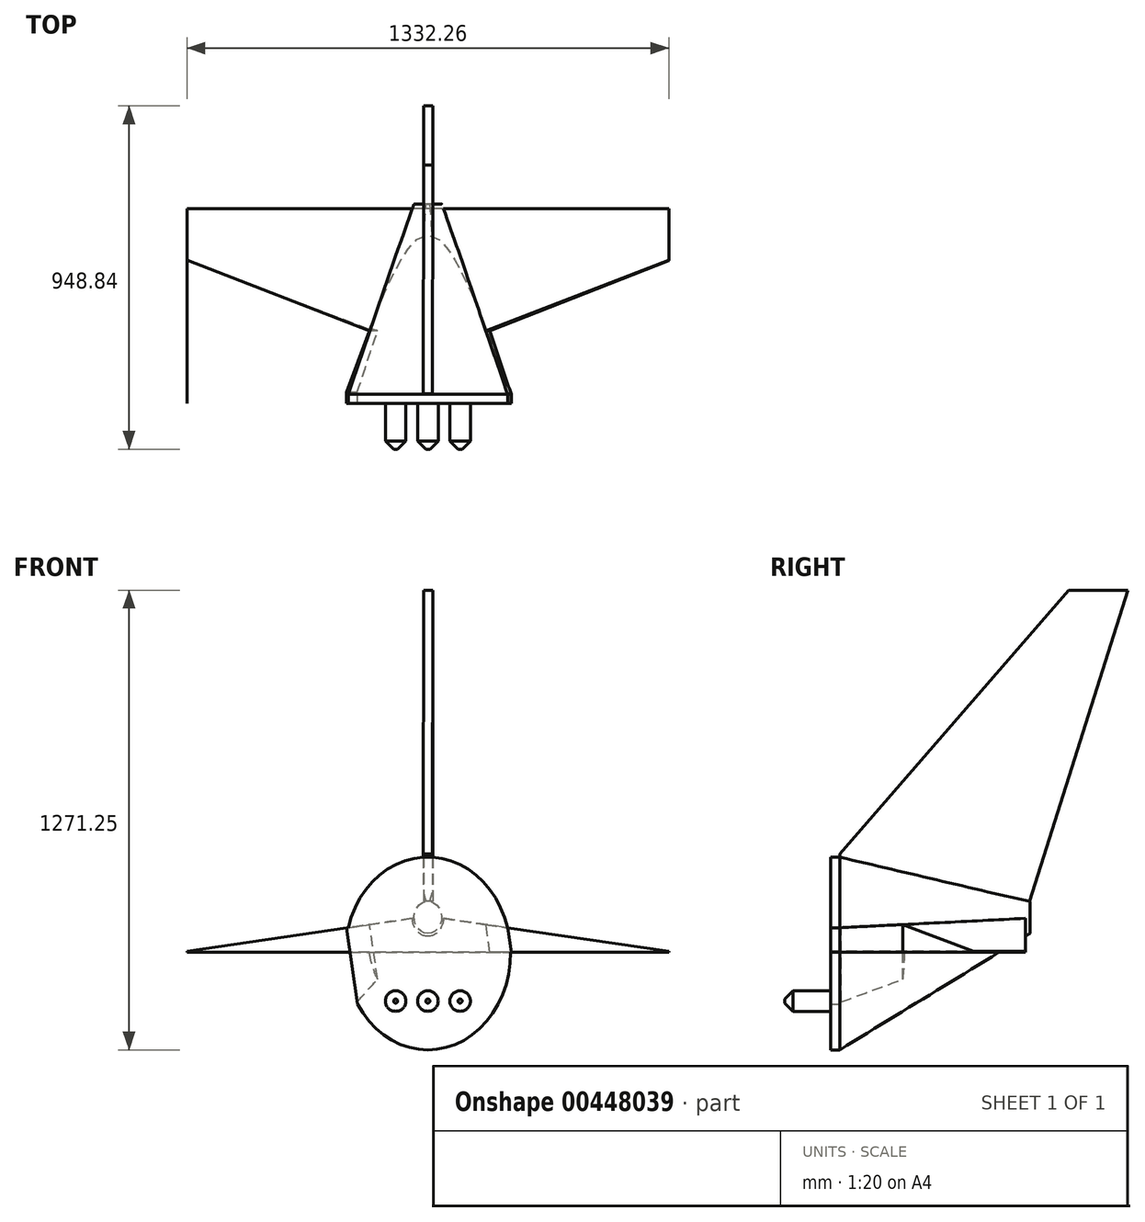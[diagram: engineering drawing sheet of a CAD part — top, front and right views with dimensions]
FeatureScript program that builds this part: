
annotation { "Feature Type Name" : "Feature", "Feature Type Description" : "" }
export const myFeature = defineFeature(function(context is Context, id is Id, definition is map)
    precondition{}
    {
        {
            var Q0;
            Q0=qCreatedBy(makeId("Front.planeOp"),FACE);
            var sketch = newSketch(context, id + "F0", { "sketchPlane" : qUnion([Q0])});
            skEllipse(sketch, "E0", {"center": v(-401.03, 615.4) * mm, "majorRadius": 266.7 * mm, "minorRadius": 228.6 * mm, "majorAxis": v(0, -1)});
            skSolve(sketch);
        }
        {
            var Q0;
            Q0=makeQuery(id+"F0.imprint","IMPRINT",FACE,{"disambiguationData":[TD([[makeQuery(id+"F0.imprint","IMPRINT",EDGE,{"derivedFrom":sQuery(id+"F0.wireOp",EDGE,"E0")}),1.0]])]});
            extrude(context, id + "F1", {"entities" : qUnion([Q0]), "depth" : 25.4 * mm});
        }
        {
            var Q0;
            Q0=makeQuery(id+"F1.opExtrude","CAP_FACE",FACE,{"disambiguationData":[OSD([sQuery(id+"F0.wireOp",EDGE,"E0")])],"isStart":true});
            cPlane(context, id + "F2", {"entities" : qUnion([Q0]), "cplaneType" : CPlaneType.OFFSET, "offset" : 525.78 * mm, "width" : 152.4 * mm, "height" : 152.4 * mm});
        }
        {
            var Q0;
            Q0=qCreatedBy(id+"F2.planeOp",FACE);
            var sketch = newSketch(context, id + "F3", { "sketchPlane" : qUnion([Q0])});
            skEllipse(sketch, "E1", {"center": v(401.03, 714.91) * mm, "majorRadius": 44.45 * mm, "minorRadius": 38.1 * mm, "majorAxis": v(0, -1)});
            skEllipse(sketch, "E2.0", {"center": v(401.03, 615.4) * mm, "majorRadius": 266.7 * mm, "minorRadius": 228.6 * mm, "majorAxis": v(0, -1)});
            skLineSegment(sketch, "E3", {"start": v(401.03, 882.1) * mm, "end": v(401.03, 348.7) * mm, "construction": true});
            skSolve(sketch);
        }
        {
            var Q0;
            Q0=makeQuery(id+"F3.imprint","IMPRINT",FACE,{"disambiguationData":[TD([[makeQuery(id+"F3.imprint","IMPRINT",EDGE,{"derivedFrom":sQuery(id+"F3.wireOp",EDGE,"E1")}),1.0]])]});
            extrude(context, id + "F4", {"entities" : qUnion([Q0]), "depth" : 0 * mm});
        }
        {
            var Q0;
            Q0=makeQuery(id+"F1.opExtrude","CAP_FACE",FACE,{"disambiguationData":[OSD([sQuery(id+"F0.wireOp",EDGE,"E0")])],"isStart":true});
            var Q1;
            Q1=makeQuery(id+"F4.opExtrude","CAP_FACE",FACE,{"disambiguationData":[OSD([sQuery(id+"F3.wireOp",EDGE,"E1")])],"isStart":false});
            loft(context, id + "F5", {"operationType" : NewBodyOperationType.ADD, "sheetProfilesArray" : [{ "sheetProfileEntities" : qUnion([Q0]) }, { "sheetProfileEntities" : qUnion([Q1]) }]});
        }
        {
            var Q0;
            Q0=makeQuery(id+"F1.opExtrude","CAP_FACE",FACE,{"disambiguationData":[OSD([sQuery(id+"F0.wireOp",EDGE,"E0")])],"isStart":false});
            var sketch = newSketch(context, id + "F6", { "sketchPlane" : qUnion([Q0])});
            skLineSegment(sketch, "E4", {"start": v(-401.03, 882.1) * mm, "end": v(-401.03, 348.7) * mm});
            skSolve(sketch);
        }
        {
            var Q0;
            Q0=makeQuery(id+"F4.opExtrude","CAP_FACE",FACE,{"disambiguationData":[OSD([sQuery(id+"F3.wireOp",EDGE,"E1")])],"isStart":false});
            var sketch = newSketch(context, id + "F7", { "sketchPlane" : qUnion([Q0])});
            skLineSegment(sketch, "E5", {"start": v(400.4, 670.47) * mm, "end": v(400.4, 759.35) * mm});
            skSolve(sketch);
        }
        {
            var Q0;
            Q0=sQuery(id+"F6.wireOp",EDGE,"E4");
            var Q1;
            Q1=sQuery(id+"F7.wireOp",EDGE,"E5");
            cPlane(context, id + "F8", {"entities" : qUnion([Q0, Q1]), "cplaneType" : CPlaneType.LINE_ANGLE, "offset" : 25.4 * mm, "angle" : 0 * degree, "width" : 152.4 * mm, "height" : 152.4 * mm});
        }
        {
            var Q0;
            Q0=qCreatedBy(id+"F8.planeOp",FACE);
            var sketch = newSketch(context, id + "F9", { "sketchPlane" : qUnion([Q0])});
            skLineSegment(sketch, "E6", {"start": v(0, 890.32) * mm, "end": v(632.36, 1619.95) * mm});
            skLineSegment(sketch, "E7", {"start": v(632.36, 1619.95) * mm, "end": v(795.96, 1619.95) * mm});
            skLineSegment(sketch, "E8", {"start": v(0, 890.32) * mm, "end": v(0, 877.57) * mm});
            skLineSegment(sketch, "E9", {"start": v(0, 877.57) * mm, "end": v(524.82, 759.1) * mm});
            skLineSegment(sketch, "E10", {"start": v(795.96, 1619.95) * mm, "end": v(524.82, 759.1) * mm});
            skSolve(sketch);
        }
        {
            var Q0;
            Q0=makeQuery(id+"F9.imprint","IMPRINT",FACE,{"disambiguationData":[TD([[makeQuery(id+"F9.imprint","IMPRINT",EDGE,{"derivedFrom":sQuery(id+"F9.wireOp",EDGE,"E6")}),-1.0]])]});
            extrude(context, id + "F10", {"entities" : qUnion([Q0]), "operationType" : NewBodyOperationType.ADD, "endBound" : BoundingType.SYMMETRIC, "depth" : 25.4 * mm, "offsetDistance" : 25.4 * mm});
        }
        {
            var Q0;
            {var subQ0=sQuery(id+"F6.wireOp",EDGE,"E4");Q0=makeQuery(id+"F6.imprint","IMPRINT",FACE,{"disambiguationData":[TD([[makeQuery(id+"F6.imprint","IMPRINT",EDGE,{"derivedFrom":subQ0}),-1.0]])]});}
            var sketch = newSketch(context, id + "F11", { "sketchPlane" : qUnion([Q0])});
            skLineSegment(sketch, "E11", {"start": v(-1067.16, 621.37) * mm, "end": v(-1067.16, 618.15) * mm});
            skEllipse(sketch, "E12.0", {"center": v(-401.03, 615.4) * mm, "majorRadius": 266.7 * mm, "minorRadius": 228.6 * mm, "majorAxis": v(0, -1)});
            skLineSegment(sketch, "E13", {"start": v(-401.03, 882.1) * mm, "end": v(-401.03, 348.7) * mm, "construction": true});
            skLineSegment(sketch, "E14", {"start": v(-1067.16, 621.37) * mm, "end": v(-401.03, 718.65) * mm});
            skLineSegment(sketch, "E15", {"start": v(-1067.16, 618.15) * mm, "end": v(-401.03, 618.15) * mm});
            skLineSegment(sketch, "E16.MirrorCS", {"start": v(265.1, 618.15) * mm, "end": v(-401.03, 618.15) * mm});
            skLineSegment(sketch, "E17.MirrorCS", {"start": v(265.1, 621.37) * mm, "end": v(265.1, 618.15) * mm});
            skLineSegment(sketch, "E18.MirrorCS", {"start": v(265.1, 621.37) * mm, "end": v(-401.03, 718.65) * mm});
            skSolve(sketch);
        }
        {
            var Q0;
            {var subQ5=sQuery(id+"F11.wireOp",EDGE,"E17.MirrorCS");Q0=makeQuery(id+"F11.imprint","IMPRINT",FACE,{"disambiguationData":[TD([[makeQuery(id+"F11.imprint","IMPRINT",EDGE,{"derivedFrom":subQ5}),-1.0]])]});}
            var Q1;
            {var subQ0=sQuery(id+"F11.wireOp",EDGE,"E11");Q1=makeQuery(id+"F11.imprint","IMPRINT",FACE,{"disambiguationData":[TD([[makeQuery(id+"F11.imprint","IMPRINT",EDGE,{"derivedFrom":subQ0}),1.0]])]});}
            var Q2;
            {var subQ0=sQuery(id+"F11.wireOp",EDGE,"E16.MirrorCS");var subQ1=sQuery(id+"F11.wireOp",EDGE,"E12.0");var subQ2=makeQuery(id+"F11.imprint","INTERSECT",VERTEX,{"derivedFrom":[subQ1,subQ0]});Q2=makeQuery(id+"F11.imprint","IMPRINT",FACE,{"disambiguationData":[TD([[makeQuery(id+"F11.imprint","IMPRINT",EDGE,{"disambiguationData":[TD([[subQ2,-1.0]])],"derivedFrom":subQ1}),1.0]])]});}
            var Q3;
            {var subQ0=sQuery(id+"F11.wireOp",EDGE,"E14");var subQ1=sQuery(id+"F11.wireOp",EDGE,"E12.0");var subQ2=makeQuery(id+"F11.imprint","INTERSECT",VERTEX,{"derivedFrom":[subQ1,subQ0]});Q3=makeQuery(id+"F11.imprint","IMPRINT",FACE,{"disambiguationData":[TD([[makeQuery(id+"F11.imprint","IMPRINT",EDGE,{"disambiguationData":[TD([[subQ2,-1.0]])],"derivedFrom":subQ1}),1.0]])]});}
            extrude(context, id + "F12", {"entities" : qUnion([Q0, Q1, Q2, Q3]), "operationType" : NewBodyOperationType.ADD, "oppositeDirection" : true, "depth" : 538.48 * mm, "offsetDistance" : 25.4 * mm});
        }
        {
            var Q0;
            Q0=makeQuery(id+"F12.opExtrude","SWEPT_FACE",FACE,{"disambiguationData":[OSD([sQuery(id+"F11.wireOp",EDGE,"E18.MirrorCS")])]});
            var sketch = newSketch(context, id + "F13", { "sketchPlane" : qUnion([Q0])});
            skLineSegment(sketch, "E19", {"start": v(-338.6, 174.72) * mm, "end": v(172.96, 369.87) * mm});
            skLineSegment(sketch, "E20", {"start": v(172.52, 477.14) * mm, "end": v(-456.7, 510.86) * mm});
            skLineSegment(sketch, "E21", {"start": v(-338.6, 174.72) * mm, "end": v(-456.7, 510.86) * mm});
            skLineSegment(sketch, "E22.0", {"start": v(-278, -25.4) * mm, "end": v(-714.04, -25.4) * mm});
            skLineSegment(sketch, "E23", {"start": v(-496.02, -25.4) * mm, "end": v(-496.02, 559.25) * mm, "construction": true});
            skLineSegment(sketch, "E24", {"start": v(172.96, 369.87) * mm, "end": v(172.52, 477.14) * mm});
            skLineSegment(sketch, "E25", {"start": v(-333.88, 174.72) * mm, "end": v(-334.48, 176.3) * mm});
            skSolve(sketch);
        }
        {
            var Q0;
            Q0=makeQuery(id+"F12.opExtrude","SWEPT_FACE",FACE,{"disambiguationData":[OSD([sQuery(id+"F11.wireOp",EDGE,"E14")])]});
            var sketch = newSketch(context, id + "F14", { "sketchPlane" : qUnion([Q0])});
            skLineSegment(sketch, "E26", {"start": v(375.22, 288.04) * mm, "end": v(-966.17, 288.04) * mm, "construction": true});
            skLineSegment(sketch, "E27", {"start": v(-966.17, 477.14) * mm, "end": v(-966.64, 369.87) * mm});
            skLineSegment(sketch, "E28", {"start": v(-966.64, 369.87) * mm, "end": v(-455.08, 174.6) * mm});
            skLineSegment(sketch, "E29", {"start": v(-966.17, 477.14) * mm, "end": v(-337, 510.72) * mm});
            skLineSegment(sketch, "E30", {"start": v(-455.62, 174.8) * mm, "end": v(-520.7, 4.33) * mm});
            skLineSegment(sketch, "E31", {"start": v(-520.7, 4.33) * mm, "end": v(-520.7, -25.4) * mm});
            skSolve(sketch);
        }
        {
            var Q0;
            {var subQ0=sQuery(id+"F11.wireOp",EDGE,"E14");var subQ4=makeQuery(id+"F12.opExtrude","CAP_EDGE",EDGE,{"disambiguationData":[OSD([subQ0])],"isStart":true});Q0=makeQuery(id+"F14.imprint","IMPRINT",FACE,{"disambiguationData":[TD([[makeQuery(id+"F14.imprint","IMPRINT",EDGE,{"derivedFrom":subQ4}),1.0]])]});}
            var Q1;
            {var subQ0=sQuery(id+"F11.wireOp",EDGE,"E18.MirrorCS");var subQ4=makeQuery(id+"F12.opExtrude","CAP_EDGE",EDGE,{"disambiguationData":[OSD([subQ0])],"isStart":true});Q1=makeQuery(id+"F13.imprint","IMPRINT",FACE,{"disambiguationData":[TD([[makeQuery(id+"F13.imprint","IMPRINT",EDGE,{"derivedFrom":subQ4}),-1.0]])]});}
            extrude(context, id + "F15", {"entities" : qUnion([Q0, Q1]), "operationType" : NewBodyOperationType.REMOVE, "endBound" : BoundingType.THROUGH_ALL, "oppositeDirection" : true, "depth" : 25.4 * mm, "offsetDistance" : 25.4 * mm});
        }
        {
            var Q0;
            {var subQ0=sQuery(id+"F6.wireOp",EDGE,"E4");Q0=makeQuery(id+"F6.imprint","IMPRINT",FACE,{"disambiguationData":[TD([[makeQuery(id+"F6.imprint","IMPRINT",EDGE,{"derivedFrom":subQ0}),1.0]])]});}
            var sketch = newSketch(context, id + "F16", { "sketchPlane" : qUnion([Q0])});
            skCircle(sketch, "E32", {"center": v(-490.08, 483.76) * mm, "radius": 28.44 * mm});
            skCircle(sketch, "E33.1.0.0", {"center": v(-401.03, 483.76) * mm, "radius": 28.44 * mm});
            skCircle(sketch, "E33.2.0.0", {"center": v(-311.98, 483.76) * mm, "radius": 28.44 * mm});
            skLineSegment(sketch, "E33.direction1", {"start": v(-490.08, 483.76) * mm, "end": v(-401.03, 483.76) * mm, "construction": true});
            skSolve(sketch);
        }
        {
            var Q0;
            Q0=makeQuery(id+"F16.imprint","IMPRINT",FACE,{"disambiguationData":[TD([[makeQuery(id+"F16.imprint","IMPRINT",EDGE,{"derivedFrom":sQuery(id+"F16.wireOp",EDGE,"E32")}),1.0]])]});
            var Q1;
            {var subQ0=sQuery(id+"F16.wireOp",EDGE,"E33.1.0.0");var subQ1=makeQuery(id+"F6.imprint","IMPRINT",EDGE,{"derivedFrom":sQuery(id+"F6.wireOp",EDGE,"E4")});var subQ2=makeQuery(id+"F16.imprint","INTERSECT",VERTEX,{"disambiguationData":[OD(0.0)],"derivedFrom":[subQ1,subQ0]});Q1=makeQuery(id+"F16.imprint","IMPRINT",FACE,{"disambiguationData":[TD([[makeQuery(id+"F16.imprint","IMPRINT",EDGE,{"disambiguationData":[TD([[subQ2,1.0]])],"derivedFrom":subQ0}),1.0]])]});}
            var Q2;
            {var subQ0=sQuery(id+"F16.wireOp",EDGE,"E33.1.0.0");var subQ1=makeQuery(id+"F6.imprint","IMPRINT",EDGE,{"derivedFrom":sQuery(id+"F6.wireOp",EDGE,"E4")});var subQ2=makeQuery(id+"F16.imprint","INTERSECT",VERTEX,{"disambiguationData":[OD(0.0)],"derivedFrom":[subQ1,subQ0]});Q2=makeQuery(id+"F16.imprint","IMPRINT",FACE,{"disambiguationData":[TD([[makeQuery(id+"F16.imprint","IMPRINT",EDGE,{"disambiguationData":[TD([[subQ2,-1.0]])],"derivedFrom":subQ0}),1.0]])]});}
            var Q3;
            Q3=makeQuery(id+"F16.imprint","IMPRINT",FACE,{"disambiguationData":[TD([[makeQuery(id+"F16.imprint","IMPRINT",EDGE,{"derivedFrom":sQuery(id+"F16.wireOp",EDGE,"E33.2.0.0")}),1.0]])]});
            extrude(context, id + "F17", {"entities" : qUnion([Q0, Q1, Q2, Q3]), "operationType" : NewBodyOperationType.ADD, "depth" : 127 * mm, "offsetDistance" : 25.4 * mm});
        }
        {
            var Q0;
            Q0=makeQuery(id+"F17.opExtrude","CAP_EDGE",EDGE,{"disambiguationData":[OSD([sQuery(id+"F16.wireOp",EDGE,"E32")])],"isStart":false});
            var Q1;
            Q1=makeQuery(id+"F17.opExtrude","CAP_FACE",FACE,{"disambiguationData":[OSD([sQuery(id+"F16.wireOp",EDGE,"E33.1.0.0")])],"isStart":false});
            var Q2;
            Q2=makeQuery(id+"F17.opExtrude","CAP_EDGE",EDGE,{"disambiguationData":[OSD([sQuery(id+"F16.wireOp",EDGE,"E33.2.0.0")])],"isStart":false});
            chamfer(context, id + "F18", {"entities" : qUnion([Q0, Q1, Q2]), "width" : 22.86 * mm, "tangentPropagation" : true});
        }
    });
